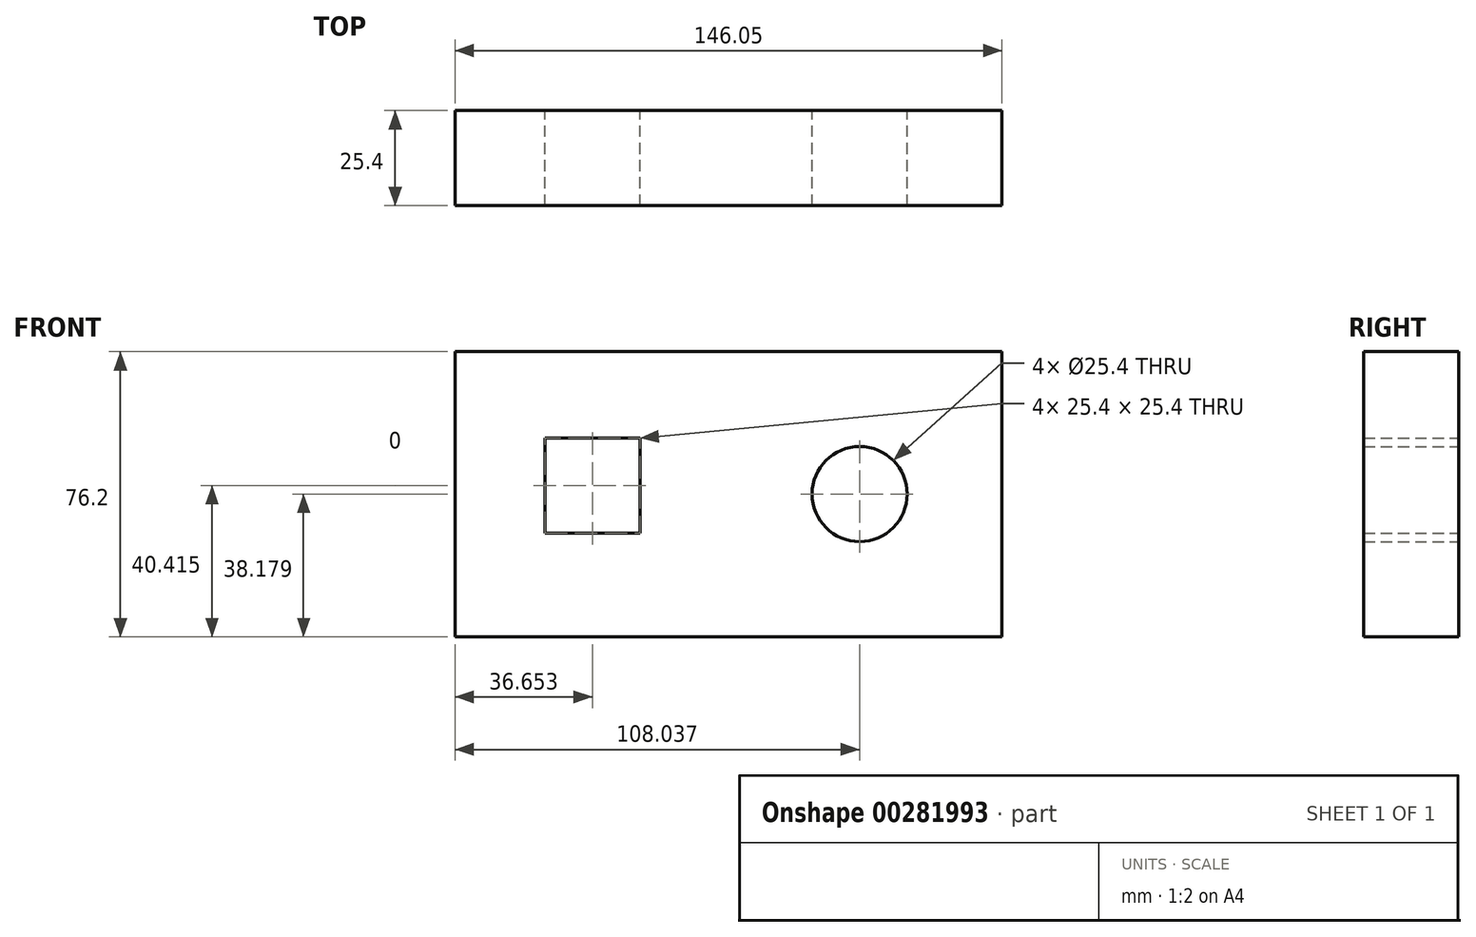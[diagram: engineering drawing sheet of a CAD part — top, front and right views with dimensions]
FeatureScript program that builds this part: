
annotation { "Feature Type Name" : "Feature", "Feature Type Description" : "" }
export const myFeature = defineFeature(function(context is Context, id is Id, definition is map)
    precondition{}
    {
        {
            var Q0;
            Q0=qCreatedBy(makeId("Front.planeOp"),FACE);
            var sketch = newSketch(context, id + "F0", { "sketchPlane" : qUnion([Q0])});
            skLineSegment(sketch, "E0.bottom", {"start": v(0, 0) * mm, "end": v(-146.05, 0) * mm});
            skLineSegment(sketch, "E0.top", {"start": v(0, 76.2) * mm, "end": v(-146.05, 76.2) * mm});
            skLineSegment(sketch, "E0.left", {"start": v(0, 0) * mm, "end": v(0, 76.2) * mm});
            skLineSegment(sketch, "E0.right", {"start": v(-146.05, 0) * mm, "end": v(-146.05, 76.2) * mm});
            skCircle(sketch, "E1", {"center": v(-38.01, 38.18) * mm, "radius": 12.7 * mm});
            skLineSegment(sketch, "E2.bottom", {"start": v(-96.7, 27.71) * mm, "end": v(-122.1, 27.71) * mm});
            skLineSegment(sketch, "E2.top", {"start": v(-96.7, 53.11) * mm, "end": v(-122.1, 53.11) * mm});
            skLineSegment(sketch, "E2.left", {"start": v(-96.7, 27.71) * mm, "end": v(-96.7, 53.11) * mm});
            skLineSegment(sketch, "E2.right", {"start": v(-122.1, 27.71) * mm, "end": v(-122.1, 53.11) * mm});
            skSolve(sketch);
        }
        {
            var Q0;
            Q0=makeQuery(id+"F0.imprint","IMPRINT",FACE,{"disambiguationData":[TD([[makeQuery(id+"F0.imprint","IMPRINT",EDGE,{"derivedFrom":sQuery(id+"F0.wireOp",EDGE,"E0.bottom")}),-1.0]])]});
            extrude(context, id + "F1", {"entities" : qUnion([Q0]), "depth" : 25.4 * mm});
        }
    });
